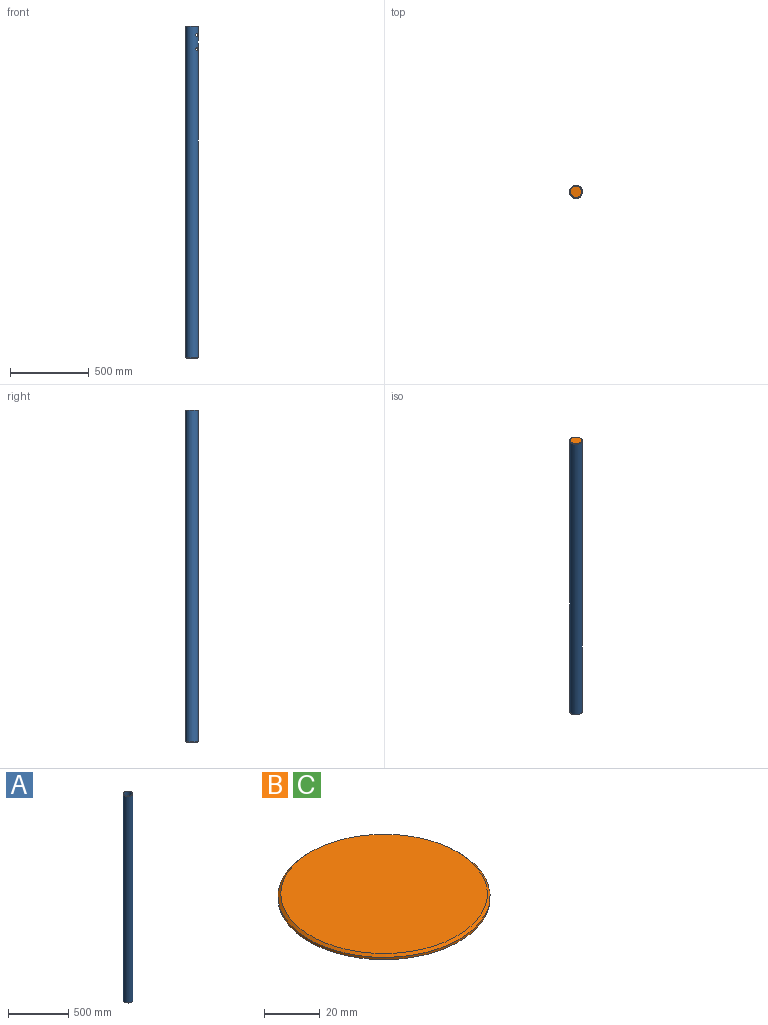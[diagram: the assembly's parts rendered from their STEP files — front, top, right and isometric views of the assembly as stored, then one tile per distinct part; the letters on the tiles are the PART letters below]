
ASSEMBLY  parts=3 mates=1
PART A: 9 faces, bbox 80x80x2100 mm
  f0: cylinder r=36mm len=2100mm, axis (0,0,-1), area 472730.3mm2, adj f2,f3,f4,f5,f6,f7,f8
  f1: cylinder r=40mm len=2100mm, axis (0,0,-1), area 525514.6mm2, adj f2,f3,f4,f5,f6,f7,f8
  f2: plane 80x80mm, normal (0,0,1), area 955mm2, adj f0,f1
  f3: plane 80x80mm, normal (0,0,-1), area 955mm2, adj f0,f1
  f4: cylinder r=16.5mm len=33mm, axis (-1,0,0), area 436.8mm2, adj f0,f1
  f5: cylinder r=10.5mm len=21mm, axis (-0.75,0.66,0), area 269.1mm2, adj f0,f1
  f6: cylinder r=10.5mm len=21mm, axis (-0.75,-0.66,0), area 269.1mm2, adj f0,f1
  f7: cylinder r=10.5mm len=21mm, axis (-0.75,-0.66,0), area 269.1mm2, adj f0,f1
  f8: cylinder r=10.5mm len=21mm, axis (-0.75,0.66,0), area 269.1mm2, adj f0,f1
PART B: 4 faces, bbox 76x76x2 mm
  f0: cylinder r=38mm len=76mm, axis (0,0,-1), area 238.8mm2, adj f2,f3
  f1: plane 74x74mm, normal (0,0,1), area 4300.8mm2, adj f3
  f2: plane 76x76mm, normal (0,0,-1), area 4536.5mm2, adj f0
  f3: cone r=37mm half-angle=45deg, axis (0,0,-1), area 333.2mm2, adj f0,f1
PART C: same geometry as B
PLACE A at identity fixed
PLACE B at identity
PLACE C rot(axis=(1,0,0),180deg) t=(0,0,1100)mm
MATE fastened C.f0 <-> A.f0  axis (0,0,1) through (0,0,-500)mm
